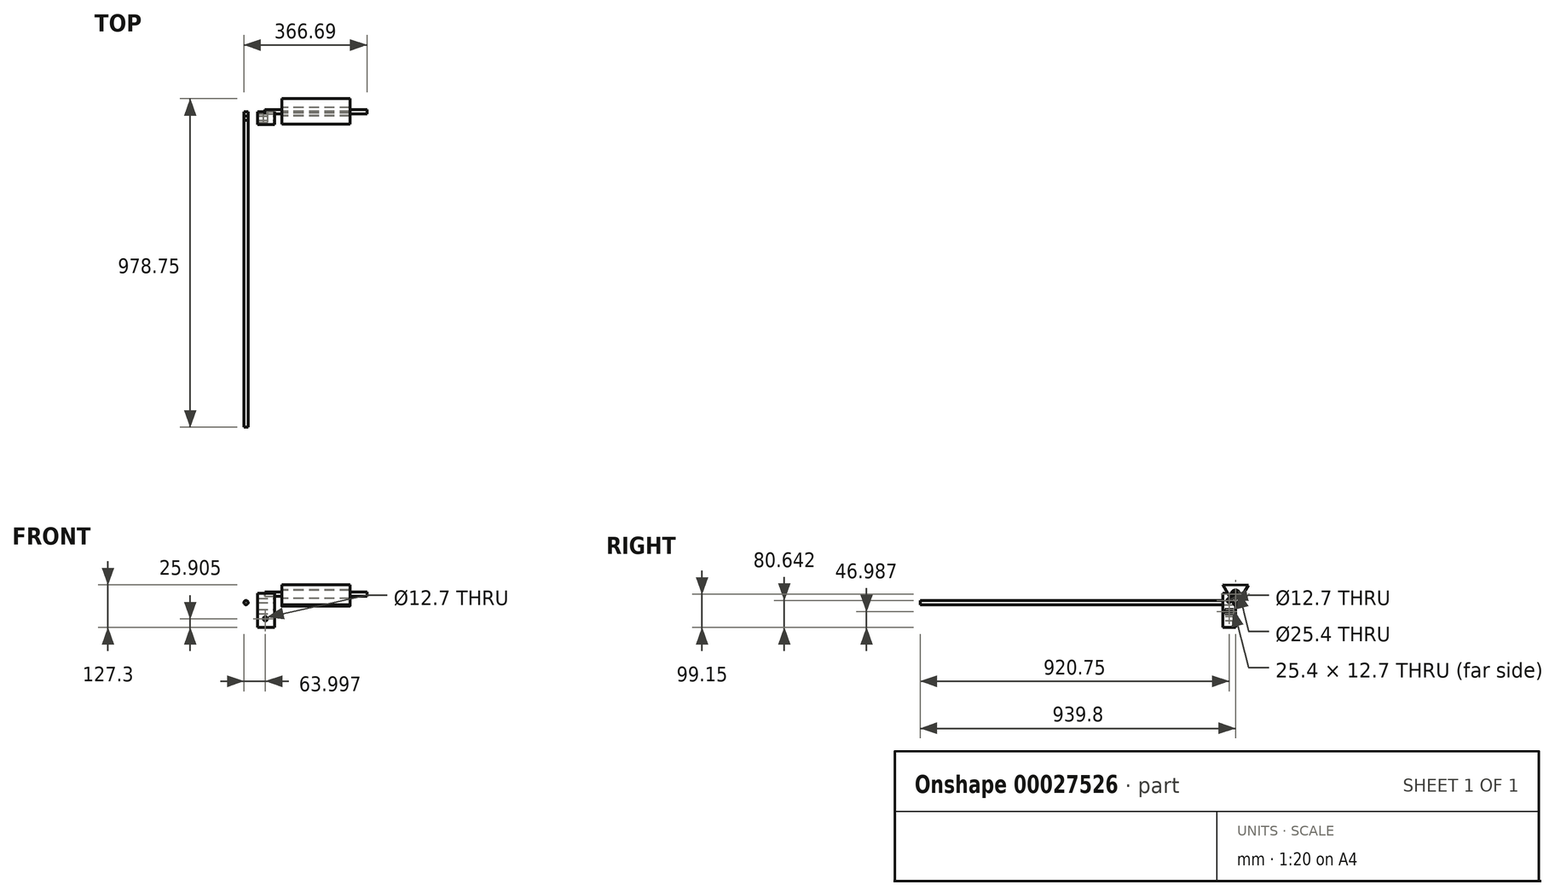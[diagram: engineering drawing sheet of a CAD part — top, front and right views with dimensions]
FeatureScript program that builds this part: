
annotation { "Feature Type Name" : "Feature", "Feature Type Description" : "" }
export const myFeature = defineFeature(function(context is Context, id is Id, definition is map)
    precondition{}
    {
        {
            var Q0;
            Q0=qCreatedBy(makeId("Right.planeOp"),FACE);
            var sketch = newSketch(context, id + "F0", { "sketchPlane" : qUnion([Q0])});
            skLineSegment(sketch, "E0", {"start": v(38.95, 27.17) * mm, "end": v(1.75, -35.38) * mm});
            skLineSegment(sketch, "E1", {"start": v(-3.66, -31.79) * mm, "end": v(-37.25, 28.15) * mm});
            skLineSegment(sketch, "E2", {"start": v(-37.25, 28.15) * mm, "end": v(38.95, 27.17) * mm});
            skFitSpline(sketch, "E3", {"points": [v(1.75, -35.38) * mm, v(0.7, -35.82) * mm, v(-3.66, -31.79) * mm], "startDerivative": vector(-3, -2.53) * mm, "endDerivative": vector(-7.25, 8.3) * mm});
            skPoint(sketch, "E4.orphan", {"position": v(0, -38.32) * mm});
            skLineSegment(sketch, "E5", {"start": v(0, 47.17) * mm, "end": v(0, -62.55) * mm, "construction": true});
            skLineSegment(sketch, "E6", {"start": v(-48.21, 0) * mm, "end": v(57.9, 0) * mm, "construction": true});
            skCircle(sketch, "E7", {"center": v(0, 0) * mm, "radius": 12.7 * mm});
            skSolve(sketch);
        }
        {
            var Q0;
            Q0=makeQuery(id+"F0.imprint","IMPRINT",FACE,{"disambiguationData":[TD([[makeQuery(id+"F0.imprint","IMPRINT",EDGE,{"derivedFrom":sQuery(id+"F0.wireOp",EDGE,"E0")}),-1.0]])]});
            extrude(context, id + "F1", {"entities" : qUnion([Q0]), "depth" : 203.2 * mm});
        }
        {
            var Q0;
            Q0=qCreatedBy(makeId("Right.planeOp"),FACE);
            var sketch = newSketch(context, id + "F2", { "sketchPlane" : qUnion([Q0])});
            skCircle(sketch, "E8", {"center": v(0, 0) * mm, "radius": 12.07 * mm});
            skSolve(sketch);
        }
        {
            var Q0;
            Q0=makeQuery(id+"F2.imprint","IMPRINT",FACE,{"disambiguationData":[TD([[makeQuery(id+"F2.imprint","IMPRINT",EDGE,{"derivedFrom":sQuery(id+"F2.wireOp",EDGE,"E8")}),1.0]])]});
            extrude(context, id + "F3", {"entities" : qUnion([Q0]), "depth" : 203.2 * mm});
        }
        {
            var Q0;
            Q0=makeQuery(id+"F3.opExtrude","CAP_FACE",FACE,{"disambiguationData":[OSD([sQuery(id+"F2.wireOp",EDGE,"E8")])],"isStart":true});
            var sketch = newSketch(context, id + "F4", { "sketchPlane" : qUnion([Q0])});
            skCircle(sketch, "E9", {"center": v(0, 0) * mm, "radius": 6.35 * mm});
            skSolve(sketch);
        }
        {
            var Q0;
            Q0=makeQuery(id+"F4.imprint","IMPRINT",FACE,{"disambiguationData":[TD([[makeQuery(id+"F4.imprint","IMPRINT",EDGE,{"derivedFrom":sQuery(id+"F4.wireOp",EDGE,"E9")}),1.0]])]});
            extrude(context, id + "F5", {"entities" : qUnion([Q0]), "operationType" : NewBodyOperationType.ADD, "depth" : 50.8 * mm});
        }
        {
            var Q0;
            Q0=makeQuery(id+"F3.opExtrude","CAP_FACE",FACE,{"disambiguationData":[OSD([sQuery(id+"F2.wireOp",EDGE,"E8")])],"isStart":false});
            var sketch = newSketch(context, id + "F6", { "sketchPlane" : qUnion([Q0])});
            skCircle(sketch, "E10", {"center": v(0, 0) * mm, "radius": 6.35 * mm});
            skSolve(sketch);
        }
        {
            var Q0;
            Q0=makeQuery(id+"F6.imprint","IMPRINT",FACE,{"disambiguationData":[TD([[makeQuery(id+"F6.imprint","IMPRINT",EDGE,{"derivedFrom":sQuery(id+"F6.wireOp",EDGE,"E10")}),1.0]])]});
            extrude(context, id + "F7", {"entities" : qUnion([Q0]), "operationType" : NewBodyOperationType.ADD, "depth" : 50.8 * mm});
        }
        {
            var Q0;
            Q0=qCreatedBy(makeId("Front.planeOp"),FACE);
            var sketch = newSketch(context, id + "F8", { "sketchPlane" : qUnion([Q0])});
            skCircle(sketch, "E11", {"center": v(-106.33, -24.94) * mm, "radius": 6.35 * mm});
            skSolve(sketch);
        }
        {
            var Q0;
            Q0=makeQuery(id+"F8.imprint","IMPRINT",FACE,{"disambiguationData":[TD([[makeQuery(id+"F8.imprint","IMPRINT",EDGE,{"derivedFrom":sQuery(id+"F8.wireOp",EDGE,"E11")}),1.0]])]});
            extrude(context, id + "F9", {"entities" : qUnion([Q0]), "depth" : 939.8 * mm});
        }
        {
            var Q0;
            Q0=qCreatedBy(makeId("Front.planeOp"),FACE);
            var sketch = newSketch(context, id + "F10", { "sketchPlane" : qUnion([Q0])});
            skLineSegment(sketch, "E12.bottom", {"start": v(-71.64, 2.45) * mm, "end": v(-20.84, 2.45) * mm});
            skLineSegment(sketch, "E12.top", {"start": v(-71.64, -99.15) * mm, "end": v(-20.84, -99.15) * mm});
            skLineSegment(sketch, "E12.left", {"start": v(-71.64, 2.45) * mm, "end": v(-71.64, -99.15) * mm});
            skLineSegment(sketch, "E12.right", {"start": v(-20.84, 2.45) * mm, "end": v(-20.84, -99.15) * mm});
            skSolve(sketch);
        }
        {
            var Q0;
            Q0=makeQuery(id+"F10.imprint","IMPRINT",FACE,{"disambiguationData":[TD([[makeQuery(id+"F10.imprint","IMPRINT",EDGE,{"derivedFrom":sQuery(id+"F10.wireOp",EDGE,"E12.bottom")}),-1.0]])]});
            extrude(context, id + "F11", {"entities" : qUnion([Q0]), "depth" : 38.1 * mm});
        }
        {
            var Q0;
            Q0=makeQuery(id+"F11.opExtrude","CAP_FACE",FACE,{"disambiguationData":[OSD([sQuery(id+"F10.wireOp",EDGE,"E12.bottom"),sQuery(id+"F10.wireOp",EDGE,"E12.top"),sQuery(id+"F10.wireOp",EDGE,"E12.left"),sQuery(id+"F10.wireOp",EDGE,"E12.right")])],"isStart":false});
            var sketch = newSketch(context, id + "F12", { "sketchPlane" : qUnion([Q0])});
            skCircle(sketch, "E13", {"center": v(-48.7, -73.24) * mm, "radius": 6.35 * mm});
            skSolve(sketch);
        }
        {
            var Q0;
            Q0=makeQuery(id+"F12.imprint","IMPRINT",FACE,{"disambiguationData":[TD([[makeQuery(id+"F12.imprint","IMPRINT",EDGE,{"derivedFrom":sQuery(id+"F12.wireOp",EDGE,"E13")}),1.0]])]});
            extrude(context, id + "F13", {"entities" : qUnion([Q0]), "operationType" : NewBodyOperationType.REMOVE, "endBound" : BoundingType.THROUGH_ALL, "oppositeDirection" : true, "depth" : 25.4 * mm});
        }
        {
            var Q0;
            Q0=makeQuery(id+"F11.opExtrude","SWEPT_FACE",FACE,{"disambiguationData":[OSD([sQuery(id+"F10.wireOp",EDGE,"E12.right")])]});
            var sketch = newSketch(context, id + "F14", { "sketchPlane" : qUnion([Q0])});
            skLineSegment(sketch, "E14.bottom", {"start": v(-31.75, -45.81) * mm, "end": v(-6.35, -45.81) * mm});
            skLineSegment(sketch, "E14.top", {"start": v(-31.75, -58.51) * mm, "end": v(-6.35, -58.51) * mm});
            skLineSegment(sketch, "E14.left", {"start": v(-31.75, -45.81) * mm, "end": v(-31.75, -58.51) * mm});
            skLineSegment(sketch, "E14.right", {"start": v(-6.35, -45.81) * mm, "end": v(-6.35, -58.51) * mm});
            skSolve(sketch);
        }
        {
            var Q0;
            Q0=makeQuery(id+"F14.imprint","IMPRINT",FACE,{"disambiguationData":[TD([[makeQuery(id+"F14.imprint","IMPRINT",EDGE,{"derivedFrom":sQuery(id+"F14.wireOp",EDGE,"E14.bottom")}),-1.0]])]});
            extrude(context, id + "F15", {"entities" : qUnion([Q0]), "operationType" : NewBodyOperationType.REMOVE, "endBound" : BoundingType.THROUGH_ALL, "oppositeDirection" : true, "depth" : 25.4 * mm});
        }
        {
            var Q0;
            Q0=makeQuery(id+"F11.opExtrude","SWEPT_FACE",FACE,{"disambiguationData":[OSD([sQuery(id+"F10.wireOp",EDGE,"E12.right")])]});
            var sketch = newSketch(context, id + "F16", { "sketchPlane" : qUnion([Q0])});
            skCircle(sketch, "E15", {"center": v(-19.05, -18.5) * mm, "radius": 6.35 * mm});
            skSolve(sketch);
        }
        {
            var Q0;
            Q0=makeQuery(id+"F16.imprint","IMPRINT",FACE,{"disambiguationData":[TD([[makeQuery(id+"F16.imprint","IMPRINT",EDGE,{"derivedFrom":sQuery(id+"F16.wireOp",EDGE,"E15")}),1.0]])]});
            extrude(context, id + "F17", {"entities" : qUnion([Q0]), "operationType" : NewBodyOperationType.REMOVE, "endBound" : BoundingType.THROUGH_ALL, "oppositeDirection" : true, "depth" : 25.4 * mm});
        }
    });
